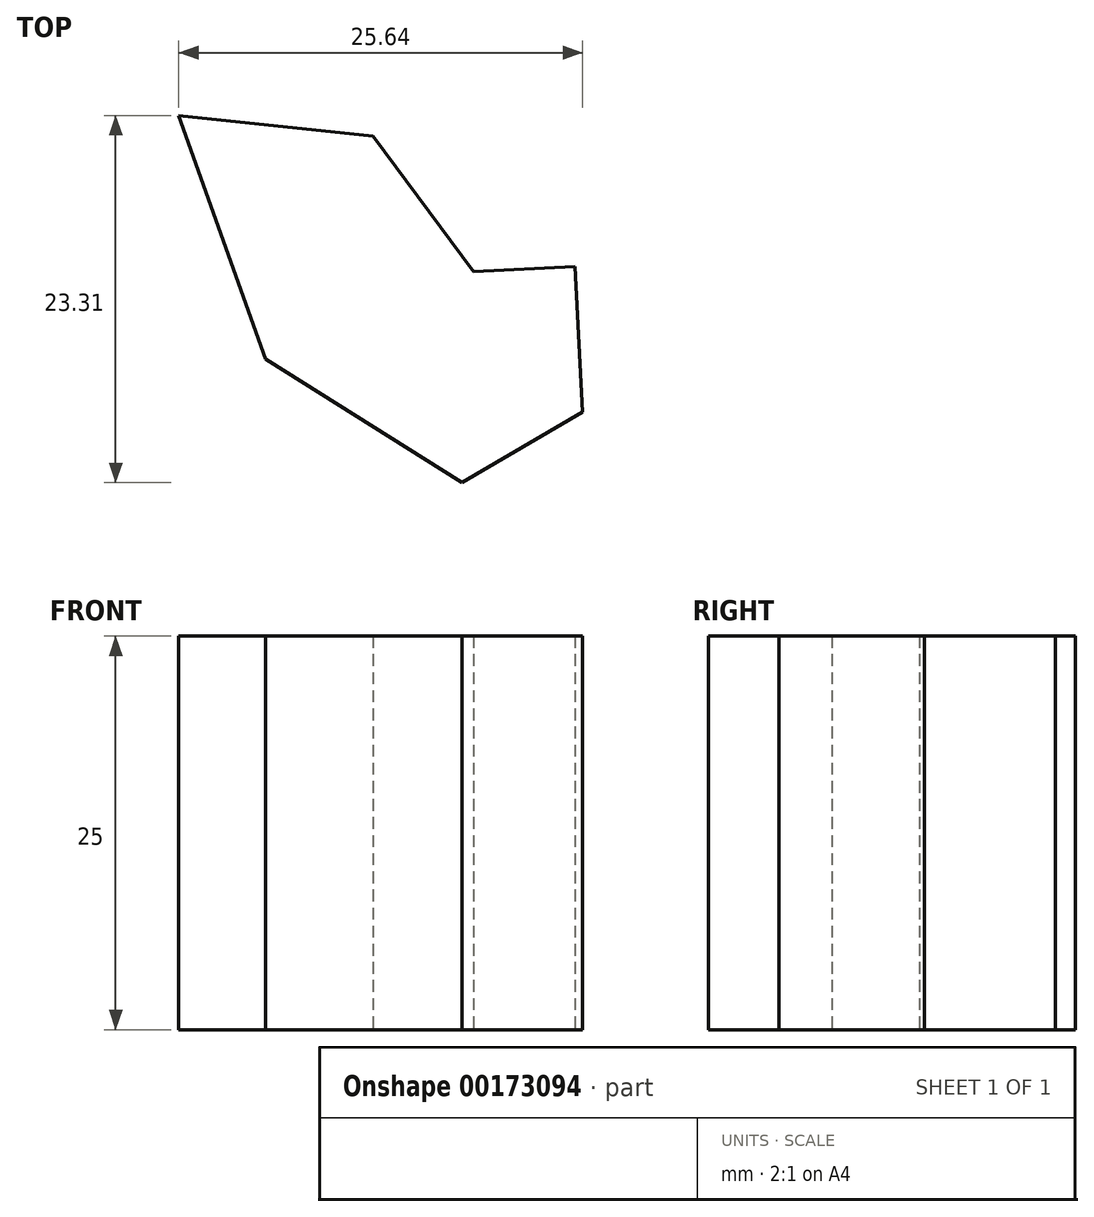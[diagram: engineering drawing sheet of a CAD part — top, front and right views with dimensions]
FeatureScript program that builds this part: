
annotation { "Feature Type Name" : "Feature", "Feature Type Description" : "" }
export const myFeature = defineFeature(function(context is Context, id is Id, definition is map)
    precondition{}
    {
        {
            var Q0;
            Q0=qCreatedBy(makeId("Top.planeOp"),FACE);
            var sketch = newSketch(context, id + "F0", { "sketchPlane" : qUnion([Q0])});
            skLineSegment(sketch, "E0", {"start": v(-13.22, 0) * mm, "end": v(-18.73, 15.46) * mm});
            skLineSegment(sketch, "E1", {"start": v(-6.4, 14.17) * mm, "end": v(-18.73, 15.46) * mm});
            skLineSegment(sketch, "E2", {"start": v(-13.22, 0) * mm, "end": v(7.41, -12.99) * mm});
            skLineSegment(sketch, "E3", {"start": v(7.41, -12.99) * mm, "end": v(6.42, 5.88) * mm});
            skLineSegment(sketch, "E4", {"start": v(6.42, 5.88) * mm, "end": v(0, 5.54) * mm});
            skLineSegment(sketch, "E5", {"start": v(0, 5.54) * mm, "end": v(-6.4, 14.17) * mm});
            skSolve(sketch);
        }
        {
            var Q0;
            Q0 = qSketchRegion(id + "F0", true);
            extrude(context, id + "F1", {"entities" : qUnion([Q0]), "depth" : 25 * mm});
        }
        {
            var Q0;
            Q0=makeQuery(id+"F1.opExtrude","SWEPT_EDGE",EDGE,{"disambiguationData":[OSD([sQuery(id+"F0.wireOp",EDGE,"E2"),sQuery(id+"F0.wireOp",EDGE,"E3")])]});
            chamfer(context, id + "F2", {"entities" : qUnion([Q0]), "width" : 5 * mm, "tangentPropagation" : true});
        }
    });
